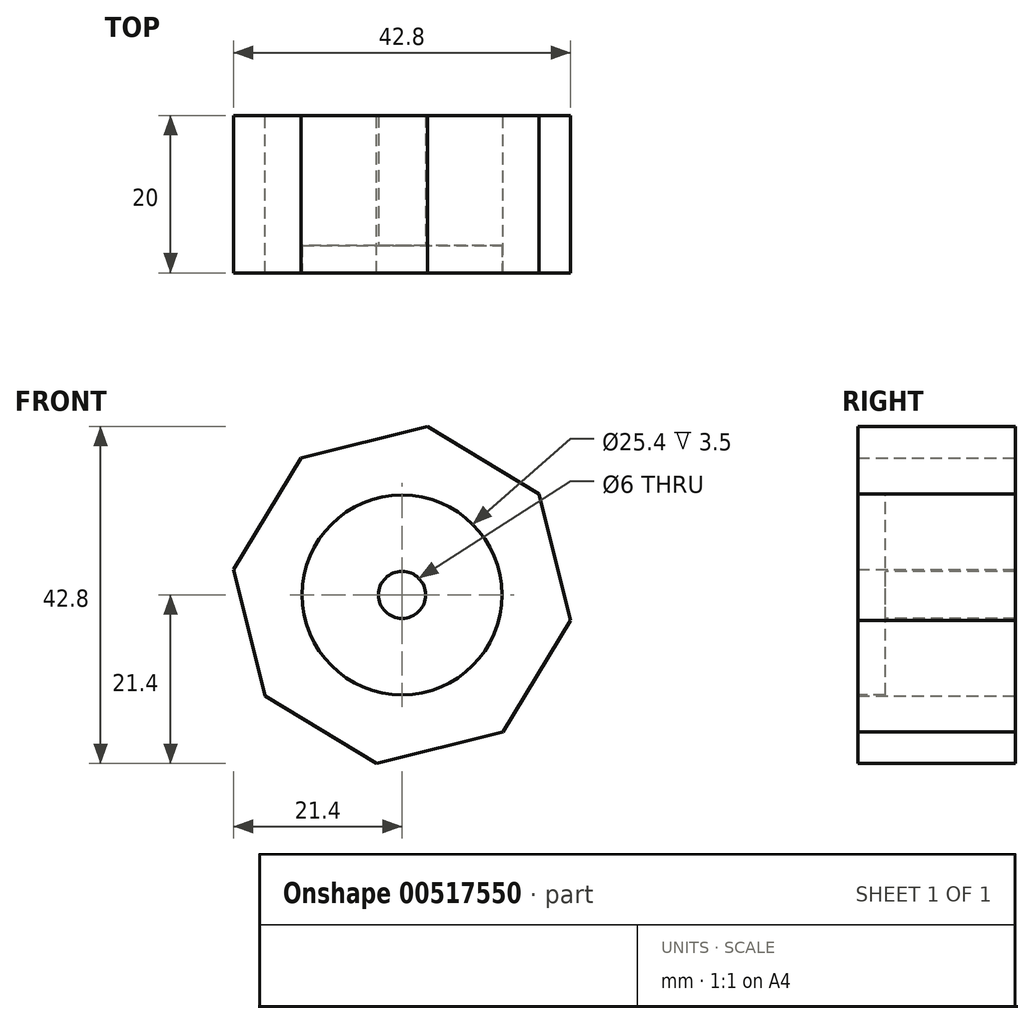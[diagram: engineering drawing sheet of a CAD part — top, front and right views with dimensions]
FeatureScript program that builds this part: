
annotation { "Feature Type Name" : "Feature", "Feature Type Description" : "" }
export const myFeature = defineFeature(function(context is Context, id is Id, definition is map)
    precondition{}
    {
        {
            var Q0;
            Q0=qCreatedBy(makeId("Front.planeOp"),FACE);
            var sketch = newSketch(context, id + "F0", { "sketchPlane" : qUnion([Q0])});
            skCircle(sketch, "E0.cCircle", {"center": v(0, 0) * mm, "radius": 20 * mm, "construction": true});
            skLineSegment(sketch, "E0.0", {"start": v(3.24, 21.4) * mm, "end": v(17.42, 12.85) * mm});
            skLineSegment(sketch, "E0.1", {"start": v(17.42, 12.85) * mm, "end": v(21.4, -3.24) * mm});
            skLineSegment(sketch, "E0.2", {"start": v(21.4, -3.24) * mm, "end": v(12.85, -17.42) * mm});
            skLineSegment(sketch, "E0.3", {"start": v(12.85, -17.42) * mm, "end": v(-3.24, -21.4) * mm});
            skLineSegment(sketch, "E0.4", {"start": v(-3.24, -21.4) * mm, "end": v(-17.42, -12.85) * mm});
            skLineSegment(sketch, "E0.5", {"start": v(-17.42, -12.85) * mm, "end": v(-21.4, 3.24) * mm});
            skLineSegment(sketch, "E0.6", {"start": v(-21.4, 3.24) * mm, "end": v(-12.85, 17.42) * mm});
            skLineSegment(sketch, "E0.7", {"start": v(-12.85, 17.42) * mm, "end": v(3.24, 21.4) * mm});
            skPoint(sketch, "E0.0.midPoint", {"position": v(10.33, 17.13) * mm});
            skSolve(sketch);
        }
        {
            var Q0;
            Q0=makeQuery(id+"F0.imprint","IMPRINT",FACE,{"disambiguationData":[TD([[makeQuery(id+"F0.imprint","IMPRINT",EDGE,{"derivedFrom":sQuery(id+"F0.wireOp",EDGE,"E0.0")}),-1.0]])]});
            extrude(context, id + "F1", {"entities" : qUnion([Q0]), "depth" : 20 * mm, "offsetDistance" : 25 * mm});
        }
        {
            var Q0;
            Q0=makeQuery(id+"F1.opExtrude","CAP_FACE",FACE,{"disambiguationData":[OSD([sQuery(id+"F0.wireOp",EDGE,"E0.0"),sQuery(id+"F0.wireOp",EDGE,"E0.1"),sQuery(id+"F0.wireOp",EDGE,"E0.2"),sQuery(id+"F0.wireOp",EDGE,"E0.3"),sQuery(id+"F0.wireOp",EDGE,"E0.4"),sQuery(id+"F0.wireOp",EDGE,"E0.5"),sQuery(id+"F0.wireOp",EDGE,"E0.6"),sQuery(id+"F0.wireOp",EDGE,"E0.7")])],"isStart":false});
            var sketch = newSketch(context, id + "F2", { "sketchPlane" : qUnion([Q0])});
            skCircle(sketch, "E1", {"center": v(0, 0) * mm, "radius": 12.7 * mm});
            skSolve(sketch);
        }
        {
            var Q0;
            Q0=makeQuery(id+"F2.imprint","IMPRINT",FACE,{"disambiguationData":[TD([[makeQuery(id+"F2.imprint","IMPRINT",EDGE,{"derivedFrom":sQuery(id+"F2.wireOp",EDGE,"E1")}),1.0]])]});
            extrude(context, id + "F3", {"entities" : qUnion([Q0]), "operationType" : NewBodyOperationType.REMOVE, "oppositeDirection" : true, "depth" : 3.5 * mm, "offsetDistance" : 25 * mm});
        }
        {
            var Q0;
            Q0=makeQuery(id+"F3.boolean.opBoolean","COPY",FACE,{"derivedFrom":makeQuery(id+"F3.opExtrude","CAP_FACE",FACE,{"disambiguationData":[OSD([sQuery(id+"F2.wireOp",EDGE,"E1")])],"isStart":false})});
            var sketch = newSketch(context, id + "F4", { "sketchPlane" : qUnion([Q0])});
            skCircle(sketch, "E2", {"center": v(0, 0) * mm, "radius": 3 * mm});
            skSolve(sketch);
        }
        {
            var Q0;
            Q0=sQuery(id+"F4.wireOp",VERTEX,"E2.center");
            var Q1;
            Q1=makeQuery(id+"F1.opExtrude","SWEPT_BODY",BODY,{"disambiguationData":[OSD([sQuery(id+"F0.wireOp",EDGE,"E0.0"),sQuery(id+"F0.wireOp",EDGE,"E0.1"),sQuery(id+"F0.wireOp",EDGE,"E0.2"),sQuery(id+"F0.wireOp",EDGE,"E0.3"),sQuery(id+"F0.wireOp",EDGE,"E0.4"),sQuery(id+"F0.wireOp",EDGE,"E0.5"),sQuery(id+"F0.wireOp",EDGE,"E0.6"),sQuery(id+"F0.wireOp",EDGE,"E0.7")])]});
            hole(context, id + "F5", {"style" : HoleStyle.SIMPLE, "endStyle" : HoleEndStyle.THROUGH, "holeDiameter" : 6 * mm, "isTappedThrough" : true, "tappedDepth" : 12 * mm, "tapClearance" : 3, "locations" : qUnion([Q0]), "scope" : qUnion([Q1])});
        }
    });
